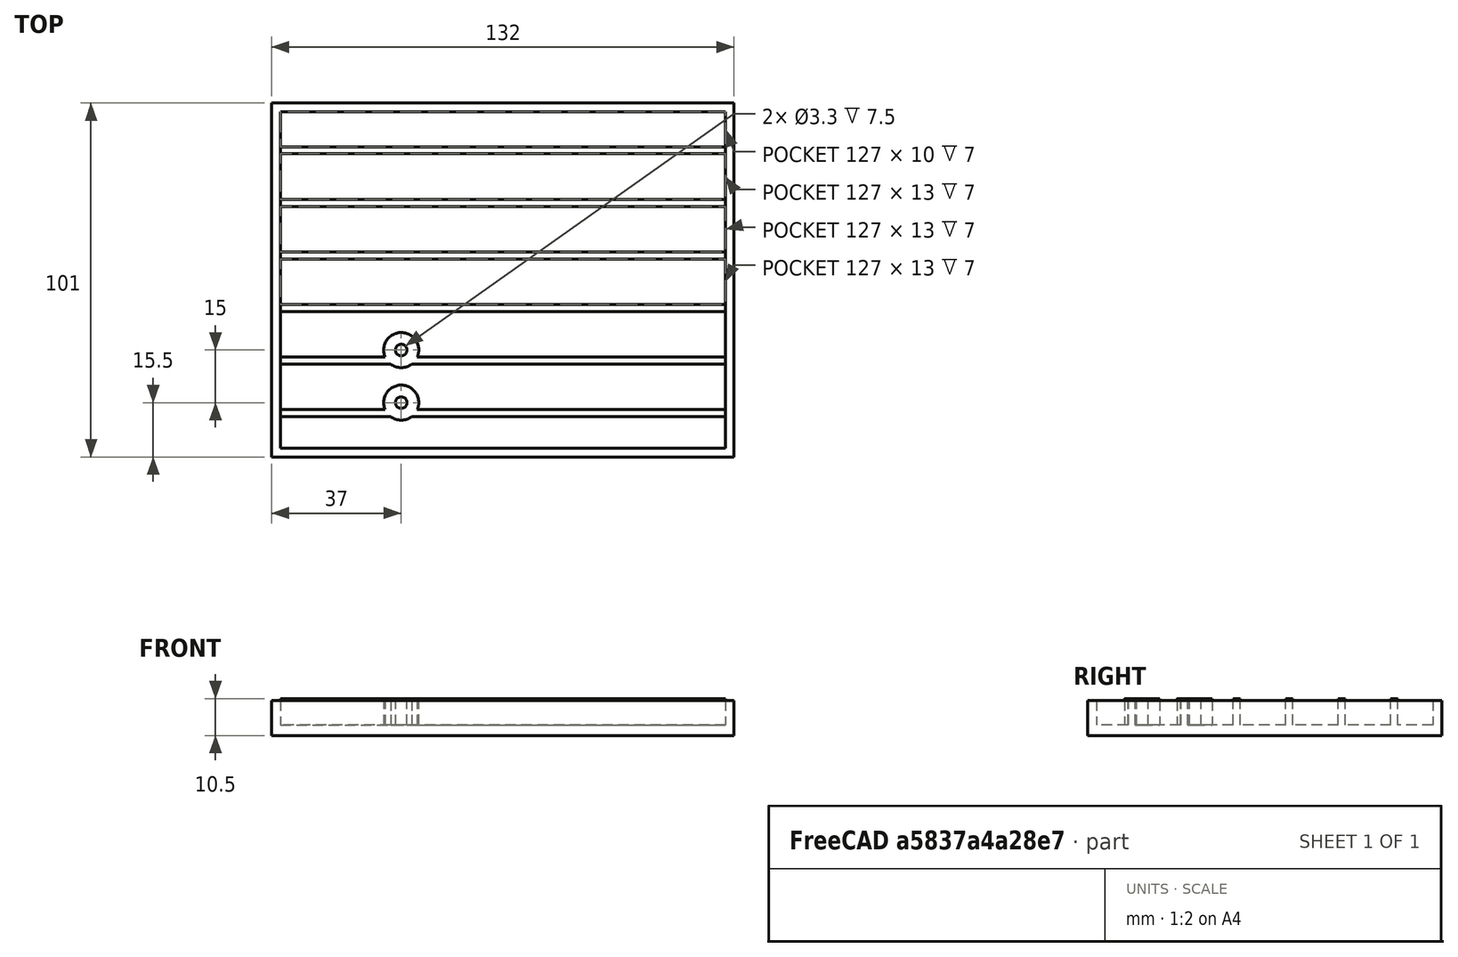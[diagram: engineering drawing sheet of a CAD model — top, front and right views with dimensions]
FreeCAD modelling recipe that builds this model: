
FCSTD DOCUMENT  (FreeCAD 0.19R24276 (Git))
Label: top
License: All rights reserved
LicenseURL: http://en.wikipedia.org/wiki/All_rights_reserved
objects: Sketcher::SketchObject×4, PartDesign::Pad×3, PartDesign::Plane×2, PartDesign::Pocket×1, Spreadsheet::Sheet×1, PartDesign::LinearPattern×1, PartDesign::Body×1, Mesh::Feature×1
note: 16 computed .brp shape members not serialized (recipe doc carries the construction recipe); baked Part::Feature solids carry a one-line shape summary decoded from their .brp

FEATURE [Sketcher::SketchObject] Sketch
  FullyConstrained = true
  MapMode = 5
  Support = -> [XY_Plane]
  expr: Constraints[10] = <<Dimensions>>.width / 2
  expr: Constraints[11] = <<Dimensions>>.length / 2
  expr: Constraints[9] = <<Dimensions>>.length
  expr: Constraints[8] = <<Dimensions>>.width
  sketch-geometry (4):
    g0: LineSegment StartX=-66 StartY=50.5 StartZ=0 EndX=66 EndY=50.5 EndZ=0
    g1: LineSegment StartX=66 StartY=50.5 StartZ=0 EndX=66 EndY=-50.5 EndZ=0
    g2: LineSegment StartX=66 StartY=-50.5 StartZ=0 EndX=-66 EndY=-50.5 EndZ=0
    g3: LineSegment StartX=-66 StartY=-50.5 StartZ=0 EndX=-66 EndY=50.5 EndZ=0
  constraints (12):
    c: Coincident(g0,g1)
    c: Coincident(g1,g2)
    c: Coincident(g2,g3)
    c: Coincident(g3,g0)
    c: Horizontal(g0)
    c: Horizontal(g2)
    c: Vertical(g1)
    c: Vertical(g3)
    c: DistanceX(g0,g0) = 132
    c: DistanceY(g1,g1) = 101
    c: Distance(g-1,g3) = 66
    c: Distance(g-1,g0) = 50.5
FEATURE [PartDesign::Pad] Pad
  AllowMultiFace = false
  Direction = (1,1,1)
  Length = 10
  Length2 = 100
  Profile = -> Sketch
  Type = 0
  expr: Length = <<Dimensions>>.height
FEATURE [PartDesign::Plane] DatumPlane
  Length = 149.083
  MapMode = 5
  Placement = pos=(0,0,10) rot=(0,0,1;0rad)
  ResizeMode = 0
  Support = -> [Pad]
  Width = 118.083
FEATURE [Sketcher::SketchObject] Sketch001
  FullyConstrained = true
  MapMode = 5
  Placement = pos=(0,0,10) rot=(0,0,1;0rad)
  Support = -> [DatumPlane]
  expr: Constraints[11] = .Constraints.inner_width / 2
  expr: Constraints[10] = .Constraints.inner_length / 2
  expr: .Constraints.inner_length = <<Dimensions>>.length - 2 * <<Dimensions>>.thickness
  expr: .Constraints.inner_width = <<Dimensions>>.width - 2 * <<Dimensions>>.thickness
  sketch-geometry (4):
    g0: LineSegment StartX=-63.5 StartY=48 StartZ=0 EndX=63.5 EndY=48 EndZ=0
    g1: LineSegment StartX=63.5 StartY=48 StartZ=0 EndX=63.5 EndY=-48 EndZ=0
    g2: LineSegment StartX=63.5 StartY=-48 StartZ=0 EndX=-63.5 EndY=-48 EndZ=0
    g3: LineSegment StartX=-63.5 StartY=-48 StartZ=0 EndX=-63.5 EndY=48 EndZ=0
  constraints (12):
    c: Coincident(g0,g1)
    c: Coincident(g1,g2)
    c: Coincident(g2,g3)
    c: Coincident(g3,g0)
    c: Horizontal(g0)
    c: Horizontal(g2)
    c: Vertical(g1)
    c: Vertical(g3)
    c: DistanceX(g0,g0) = 127  'inner_width'
    c: DistanceY(g1,g1) = 96  'inner_length'
    c: Distance(g-1,g0) = 48
    c: Distance(g-1,g1) = 63.5
FEATURE [PartDesign::Pocket] Pocket
  AllowMultiFace = false
  BaseFeature = -> Pad
  Length = 7
  Length2 = 100
  Profile = -> Sketch001
  Type = 0
FEATURE [PartDesign::Plane] DatumPlane001
  Length = 149.083
  MapMode = 5
  Placement = pos=(0,0,3) rot=(0,0,1;0rad)
  ResizeMode = 0
  Support = -> [Pocket]
  Width = 118.083
FEATURE [Sketcher::SketchObject] Sketch002
  ExternalGeometry = -> [Sketch001]
  FullyConstrained = false
  MapMode = 5
  Placement = pos=(0,0,3) rot=(0,0,1;0rad)
  Support = -> [DatumPlane001]
  expr: Constraints[9] = 3.3 / 2
  expr: Constraints[11] = <<Dimensions>>.standoff_offset
  sketch-geometry (5):
    g0: Circle CenterX=-29 CenterY=-35 CenterZ=0 NormalX=0 NormalY=0 NormalZ=1 AngleXU=0 Radius=5
    g1: Circle CenterX=-29 CenterY=-20 CenterZ=0 NormalX=0 NormalY=0 NormalZ=1 AngleXU=0 Radius=5
    g2: LineSegment StartX=-29 StartY=-14.5846 StartZ=0 EndX=-29 EndY=-39.6431 EndZ=0
    g3: Circle CenterX=-29 CenterY=-20 CenterZ=0 NormalX=0 NormalY=0 NormalZ=1 AngleXU=0 Radius=1.65
    g4: Circle CenterX=-29 CenterY=-35 CenterZ=0 NormalX=0 NormalY=0 NormalZ=1 AngleXU=0 Radius=1.65
  constraints (12):
    c: Radius(g0) = 5
    c: Equal(g0,g1)
    c: Distance(g1,g0) = 15
    c: Vertical(g2)
    c: PointOnObject(g1,g2)
    c: PointOnObject(g0,g2)
    c: Distance(g0,g-1) = 35
    c: Coincident(g3,g1)
    c: Coincident(g4,g0)
    c: Radius(g4) = 1.65
    c: Equal(g4,g3)
    c: Distance(g2,g-2) = 29
FEATURE [PartDesign::Pad] Pad001
  AllowMultiFace = false
  BaseFeature = -> Pocket
  Direction = (1,1,1)
  Length = 7.5
  Length2 = 100
  Profile = -> Sketch002
  Type = 0
  expr: Length = <<Dimensions>>.height - <<Dimensions>>.thickness
FEATURE [Spreadsheet::Sheet] Spreadsheet  label="Dimensions"
  cells = A1=Width; B1(width)==bottom_width + 2 * margin + 2 * bottom_thickness; A2=Length; B2(length)==bottom_length + 2 * margin + 2 * bottom_thickness; A3=Thickness; B3(thickness)==2.5mm; A4=Height; B4(height)==10mm; A6=Bottom width; B6(bottom_width)==125mm; A7=Bottom length; B7(bottom_length)==94mm; A8=Bottom thickness; B8(bottom_thickness)==2.5mm; A9=Margin; B9(margin)==1mm; A10=Standoff offset; B10(standoff_offset)==29mm
FEATURE [Sketcher::SketchObject] Sketch003
  ExternalGeometry = -> [Sketch001]
  FullyConstrained = true
  MapMode = 5
  Placement = pos=(0,0,3) rot=(0,0,1;0rad)
  Support = -> [DatumPlane001]
  sketch-geometry (4):
    g0: LineSegment StartX=-63.5 StartY=38 StartZ=0 EndX=63.5 EndY=38 EndZ=0
    g1: LineSegment StartX=63.5 StartY=38 StartZ=0 EndX=63.5 EndY=36 EndZ=0
    g2: LineSegment StartX=63.5 StartY=36 StartZ=0 EndX=-63.5 EndY=36 EndZ=0
    g3: LineSegment StartX=-63.5 StartY=36 StartZ=0 EndX=-63.5 EndY=38 EndZ=0
  constraints (12):
    c: Coincident(g0,g1)
    c: Coincident(g1,g2)
    c: Coincident(g2,g3)
    c: Coincident(g3,g0)
    c: Horizontal(g0)
    c: Horizontal(g2)
    c: Vertical(g1)
    c: Vertical(g3)
    c: PointOnObject(g0,g-3)
    c: PointOnObject(g1,g-5)
    c: DistanceY(g1,g1) = 2
    c: Distance(g0,g-4) = 10
FEATURE [PartDesign::Pad] Pad002
  BaseFeature = -> Pad001
  Direction = (1,1,1)
  Length = 7.5
  Length2 = 100
  Profile = -> Sketch003
  Type = 0
  expr: Length = <<Dimensions>>.height - <<Dimensions>>.thickness
FEATURE [PartDesign::LinearPattern] LinearPattern
  BaseFeature = -> Pad002
  Direction = -> Sketch003 [V_Axis]
  Length = 75
  Occurrences = 6
  Originals = -> [Pad002]
  Reversed = true
FEATURE [PartDesign::Body] Body
  Group = -> [Sketch,Pad,DatumPlane,Sketch001,Pocket,DatumPlane001,Sketch002,Pad001,Sketch003,Pad002,LinearPattern]
  Origin = -> Origin
  Tip = -> LinearPattern
FEATURE [Mesh::Feature] Mesh  label="Body (Meshed)"
